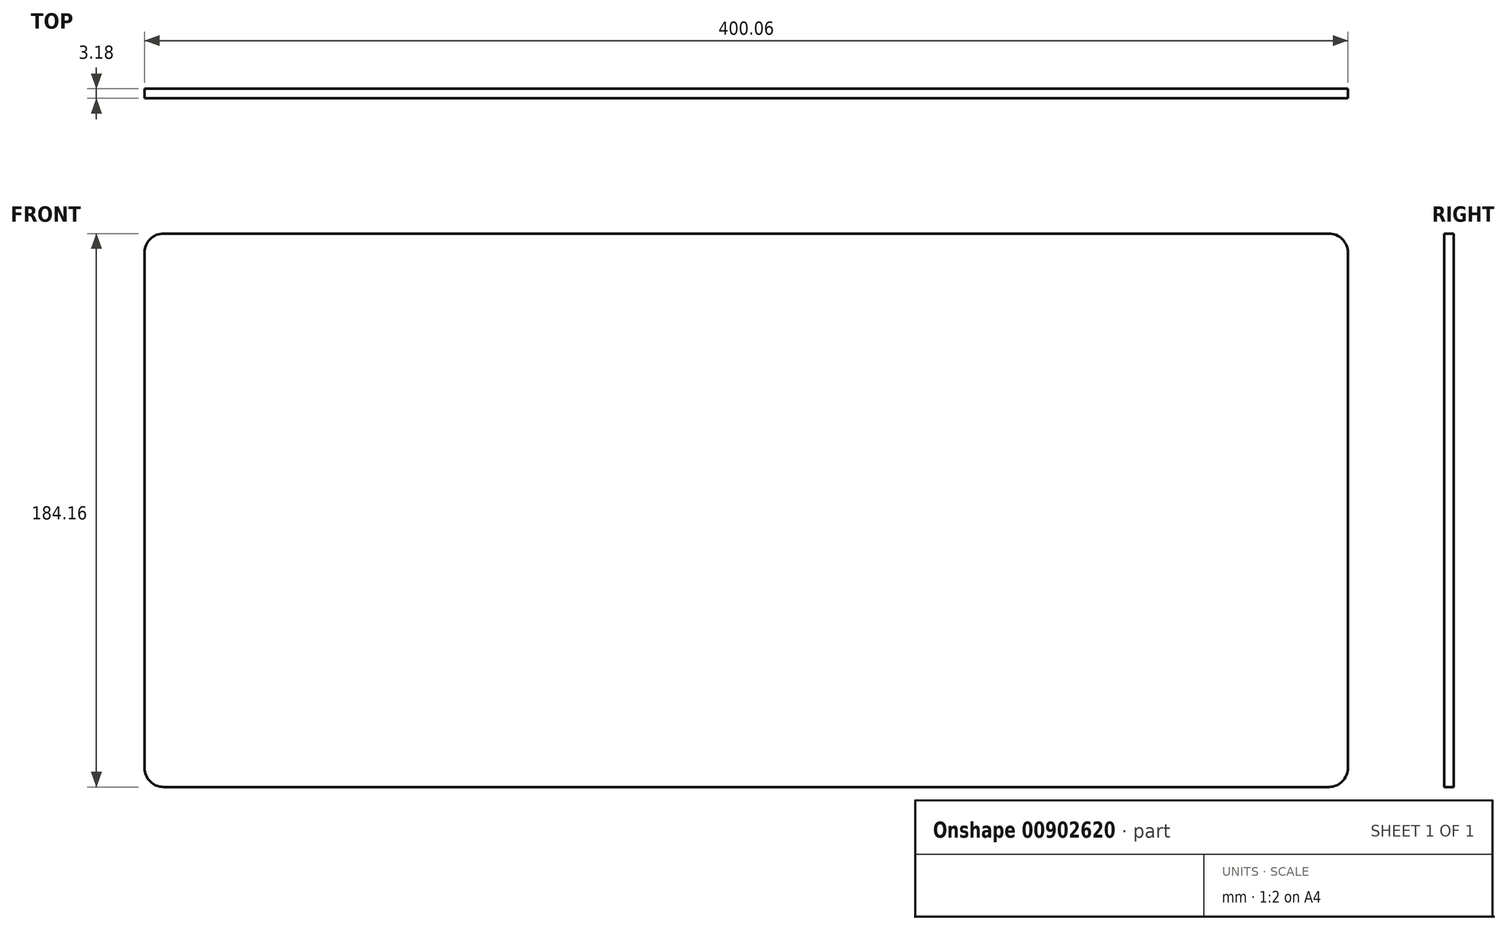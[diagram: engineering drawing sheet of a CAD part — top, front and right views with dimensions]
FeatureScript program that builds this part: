
annotation { "Feature Type Name" : "Feature", "Feature Type Description" : "" }
export const myFeature = defineFeature(function(context is Context, id is Id, definition is map)
    precondition{}
    {
        {
            var Q0;
            Q0=qCreatedBy(makeId("Front.planeOp"),FACE);
            var sketch = newSketch(context, id + "F0", { "sketchPlane" : qUnion([Q0])});
            skLineSegment(sketch, "E0.bottom", {"start": v(193.68, -92.07) * mm, "end": v(-193.68, -92.08) * mm});
            skLineSegment(sketch, "E0.top", {"start": v(193.67, 92.08) * mm, "end": v(-193.68, 92.08) * mm});
            skLineSegment(sketch, "E0.left", {"start": v(200.03, -85.72) * mm, "end": v(200.02, 85.73) * mm});
            skLineSegment(sketch, "E0.right", {"start": v(-200.03, -85.73) * mm, "end": v(-200.03, 85.73) * mm});
            skPoint(sketch, "E0.middle", {"position": v(0, 0) * mm});
            skPoint(sketch, "E1.visualSharp", {"position": v(200.02, 92.08) * mm});
            skArc(sketch, "E1.filletArc", {"start": v(200.02, 85.73) * mm, "mid": v(198.17, 90.22) * mm, "end": v(193.67, 92.07) * mm});
            skPoint(sketch, "E2.visualSharp", {"position": v(200.03, -92.07) * mm});
            skArc(sketch, "E2.filletArc", {"start": v(193.68, -92.07) * mm, "mid": v(198.17, -90.22) * mm, "end": v(200.03, -85.72) * mm});
            skPoint(sketch, "E3.visualSharp", {"position": v(-200.03, -92.08) * mm});
            skArc(sketch, "E3.filletArc", {"start": v(-200.02, -85.73) * mm, "mid": v(-198.17, -90.22) * mm, "end": v(-193.68, -92.07) * mm});
            skPoint(sketch, "E4.visualSharp", {"position": v(-200.03, 92.08) * mm});
            skArc(sketch, "E4.filletArc", {"start": v(-193.68, 92.08) * mm, "mid": v(-198.17, 90.22) * mm, "end": v(-200.03, 85.73) * mm});
            skSolve(sketch);
        }
        {
            var Q0;
            Q0=makeQuery(id+"F0.imprint","IMPRINT",FACE,{"disambiguationData":[TD([[makeQuery(id+"F0.imprint","IMPRINT",EDGE,{"derivedFrom":sQuery(id+"F0.wireOp",EDGE,"E0.bottom")}),-1.0]])]});
            extrude(context, id + "F1", {"entities" : qUnion([Q0]), "endBound" : BoundingType.SYMMETRIC, "depth" : 3.17 * mm, "offsetDistance" : 25.4 * mm});
        }
    });
